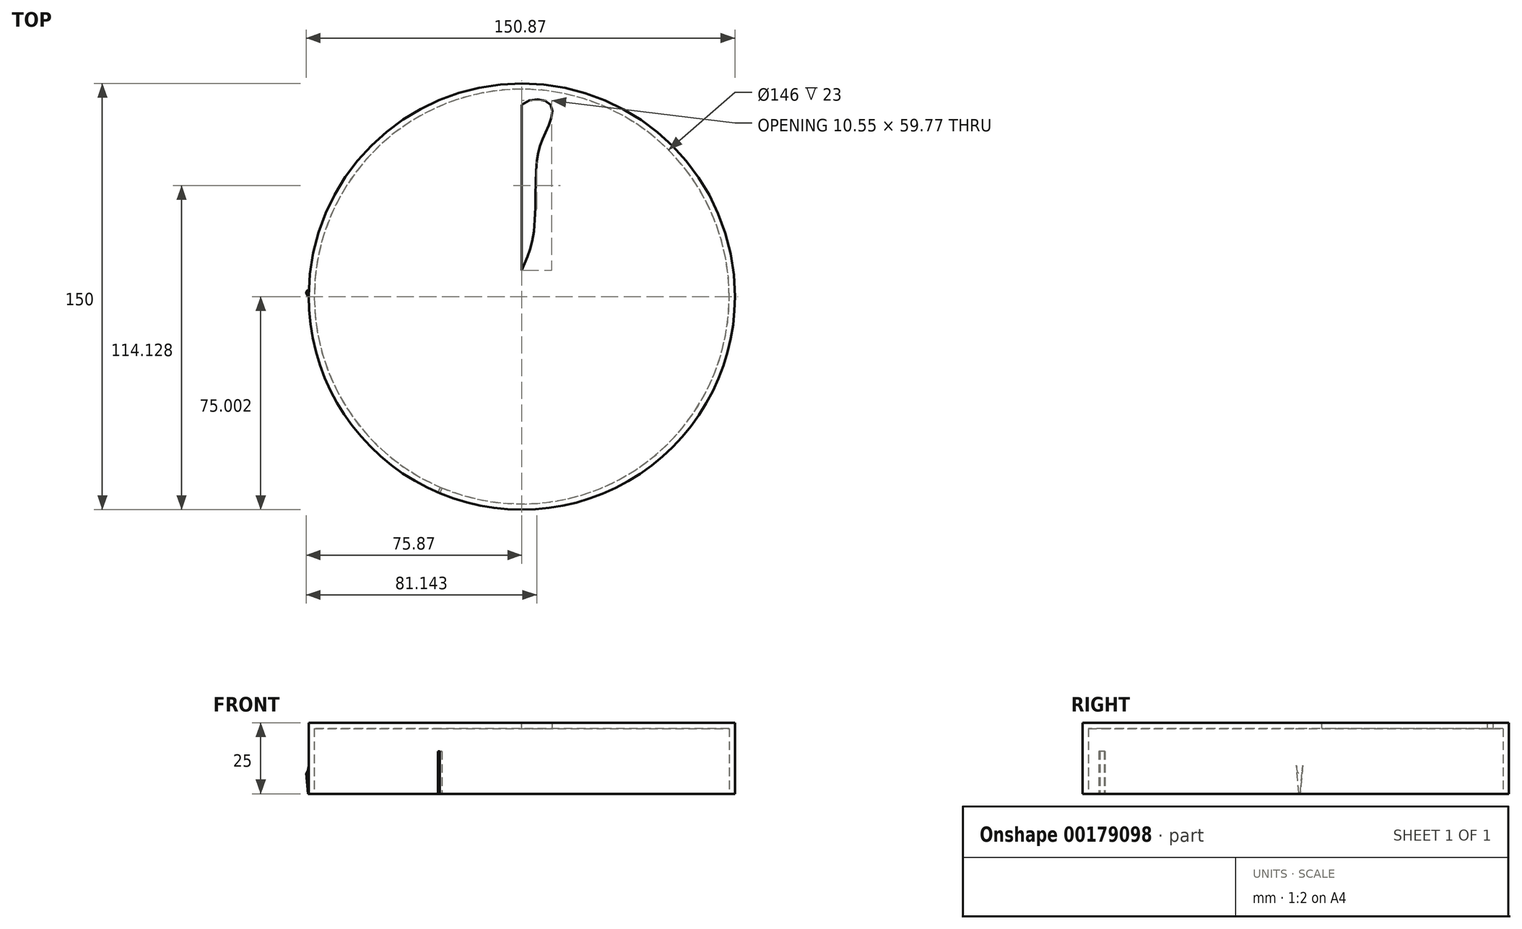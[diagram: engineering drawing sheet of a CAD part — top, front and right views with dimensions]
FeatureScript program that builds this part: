
annotation { "Feature Type Name" : "Feature", "Feature Type Description" : "" }
export const myFeature = defineFeature(function(context is Context, id is Id, definition is map)
    precondition{}
    {
        {
            var Q0;
            Q0=qCreatedBy(makeId("Top.planeOp"),FACE);
            var sketch = newSketch(context, id + "F0", { "sketchPlane" : qUnion([Q0])});
            skCircle(sketch, "E0", {"center": v(0, -1.36) * mm, "radius": 75 * mm});
            skSolve(sketch);
        }
        {
            var Q0;
            Q0=makeQuery(id+"F0.imprint","IMPRINT",FACE,{"disambiguationData":[TD([[makeQuery(id+"F0.imprint","IMPRINT",EDGE,{"derivedFrom":sQuery(id+"F0.wireOp",EDGE,"E0")}),1.0]])]});
            extrude(context, id + "F1", {"entities" : qUnion([Q0]), "depth" : 25 * mm});
        }
        {
            var Q0;
            Q0=makeQuery(id+"F1.opExtrude","CAP_FACE",FACE,{"disambiguationData":[OSD([sQuery(id+"F0.wireOp",EDGE,"E0")])],"isStart":true});
            shell(context, id + "F2", {"entities" : qUnion([Q0]), "thickness" : 2 * mm});
        }
        {
            var Q0;
            Q0=makeQuery(id+"F1.opExtrude","CAP_FACE",FACE,{"disambiguationData":[OSD([sQuery(id+"F0.wireOp",EDGE,"E0")])],"isStart":false});
            var sketch = newSketch(context, id + "F3", { "sketchPlane" : qUnion([Q0])});
            skLineSegment(sketch, "E1", {"start": v(0, 7.88) * mm, "end": v(0, 66.11) * mm});
            skFitSpline(sketch, "E2", {"points": [v(0, 66.11) * mm, v(10.1, 66.11) * mm, v(8.4, 56.52) * mm, v(5.3, 46.25) * mm, v(3.94, 19.53) * mm, v(0, 7.88) * mm], "startDerivative": vector(53.72, 50.9) * mm, "endDerivative": vector(-21.09, -57.94) * mm});
            skSolve(sketch);
        }
        {
            var Q0;
            Q0 = qSketchRegion(id + "F3", true);
            extrude(context, id + "F4", {"entities" : qUnion([Q0]), "operationType" : NewBodyOperationType.REMOVE, "endBound" : BoundingType.THROUGH_ALL, "oppositeDirection" : true, "depth" : 25 * mm});
        }
        {
            var Q0;
            Q0=qCreatedBy(makeId("Right.planeOp"),FACE);
            var sketch = newSketch(context, id + "F5", { "sketchPlane" : qUnion([Q0])});
            skLineSegment(sketch, "E3", {"start": v(0, 70.77) * mm, "end": v(0, -55.16) * mm, "construction": true});
            skSolve(sketch);
        }
        {
            var Q0;
            Q0=qCreatedBy(makeId("Top.planeOp"),FACE);
            var sketch = newSketch(context, id + "F6", { "sketchPlane" : qUnion([Q0])});
            skCircle(sketch, "E4", {"center": v(-74.99, 0) * mm, "radius": 0.25 * mm});
            skCircle(sketch, "E5.0", {"center": v(0, -1.36) * mm, "radius": 75 * mm});
            skSolve(sketch);
        }
        {
            var Q0;
            {var subQ0=sQuery(id+"F6.wireOp",EDGE,"E5.0");var subQ1=sQuery(id+"F6.wireOp",EDGE,"E4");var subQ2=makeQuery(id+"F6.imprint","INTERSECT",VERTEX,{"disambiguationData":[OD(0.0)],"derivedFrom":[subQ1,subQ0]});Q0=makeQuery(id+"F6.imprint","IMPRINT",FACE,{"disambiguationData":[TD([[makeQuery(id+"F6.imprint","IMPRINT",EDGE,{"disambiguationData":[TD([[subQ2,1.0]])],"derivedFrom":subQ1}),1.0]])]});}
            extrude(context, id + "F7", {"entities" : qUnion([Q0]), "operationType" : NewBodyOperationType.ADD, "depth" : 5 * mm, "hasDraft" : true, "draftAngle" : 5 * degree});
        }
        {
            var Q0;
            Q0=makeQuery(id+"F7.boolean.opBoolean","INTERSECT",EDGE,{"derivedFrom":[makeQuery(id+"F1.opExtrude","SWEPT_FACE",FACE,{"disambiguationData":[OSD([sQuery(id+"F0.wireOp",EDGE,"E0")])]}),makeQuery(id+"F7.opExtrude","CAP_FACE",FACE,{"disambiguationData":[OSD([sQuery(id+"F6.wireOp",EDGE,"E4"),sQuery(id+"F6.wireOp",EDGE,"E5.0")])],"isStart":false})]});
            fillet(context, id + "F8", {"entities" : qUnion([Q0]), "radius" : 5 * mm, "tangentPropagation" : true, "allowEdgeOverflow" : false});
        }
        {
            var Q0;
            {var subQ0=sQuery(id+"F6.wireOp",EDGE,"E5.0");var subQ1=sQuery(id+"F6.wireOp",EDGE,"E4");var subQ2=makeQuery(id+"F6.imprint","INTERSECT",VERTEX,{"disambiguationData":[OD(0.0)],"derivedFrom":[subQ1,subQ0]});Q0=makeQuery(id+"F6.imprint","IMPRINT",FACE,{"disambiguationData":[TD([[makeQuery(id+"F6.imprint","IMPRINT",EDGE,{"disambiguationData":[TD([[subQ2,-1.0]])],"derivedFrom":subQ1}),-1.0]])]});}
            var sketch = newSketch(context, id + "F9", { "sketchPlane" : qUnion([Q0])});
            skLineSegment(sketch, "E6", {"start": v(0, 0) * mm, "end": v(-31.45, -75.92) * mm, "construction": true});
            skLineSegment(sketch, "E7.bottom", {"start": v(-27.14, -66.54) * mm, "end": v(-27.86, -66.24) * mm});
            skLineSegment(sketch, "E7.top", {"start": v(-29.87, -73.15) * mm, "end": v(-30.6, -72.85) * mm});
            skLineSegment(sketch, "E7.left", {"start": v(-27.14, -66.54) * mm, "end": v(-29.87, -73.15) * mm});
            skLineSegment(sketch, "E7.right", {"start": v(-27.86, -66.24) * mm, "end": v(-30.6, -72.85) * mm});
            skPoint(sketch, "E7.middle", {"position": v(-28.87, -69.7) * mm});
            skSolve(sketch);
        }
        {
            var Q0;
            {var subQ0=sQuery(id+"F9.wireOp",EDGE,"E7.bottom");Q0=makeQuery(id+"F9.imprint","IMPRINT",FACE,{"disambiguationData":[TD([[makeQuery(id+"F9.imprint","IMPRINT",EDGE,{"derivedFrom":subQ0}),1.0]])]});}
            extrude(context, id + "F10", {"entities" : qUnion([Q0]), "operationType" : NewBodyOperationType.REMOVE, "depth" : 15 * mm});
        }
    });
